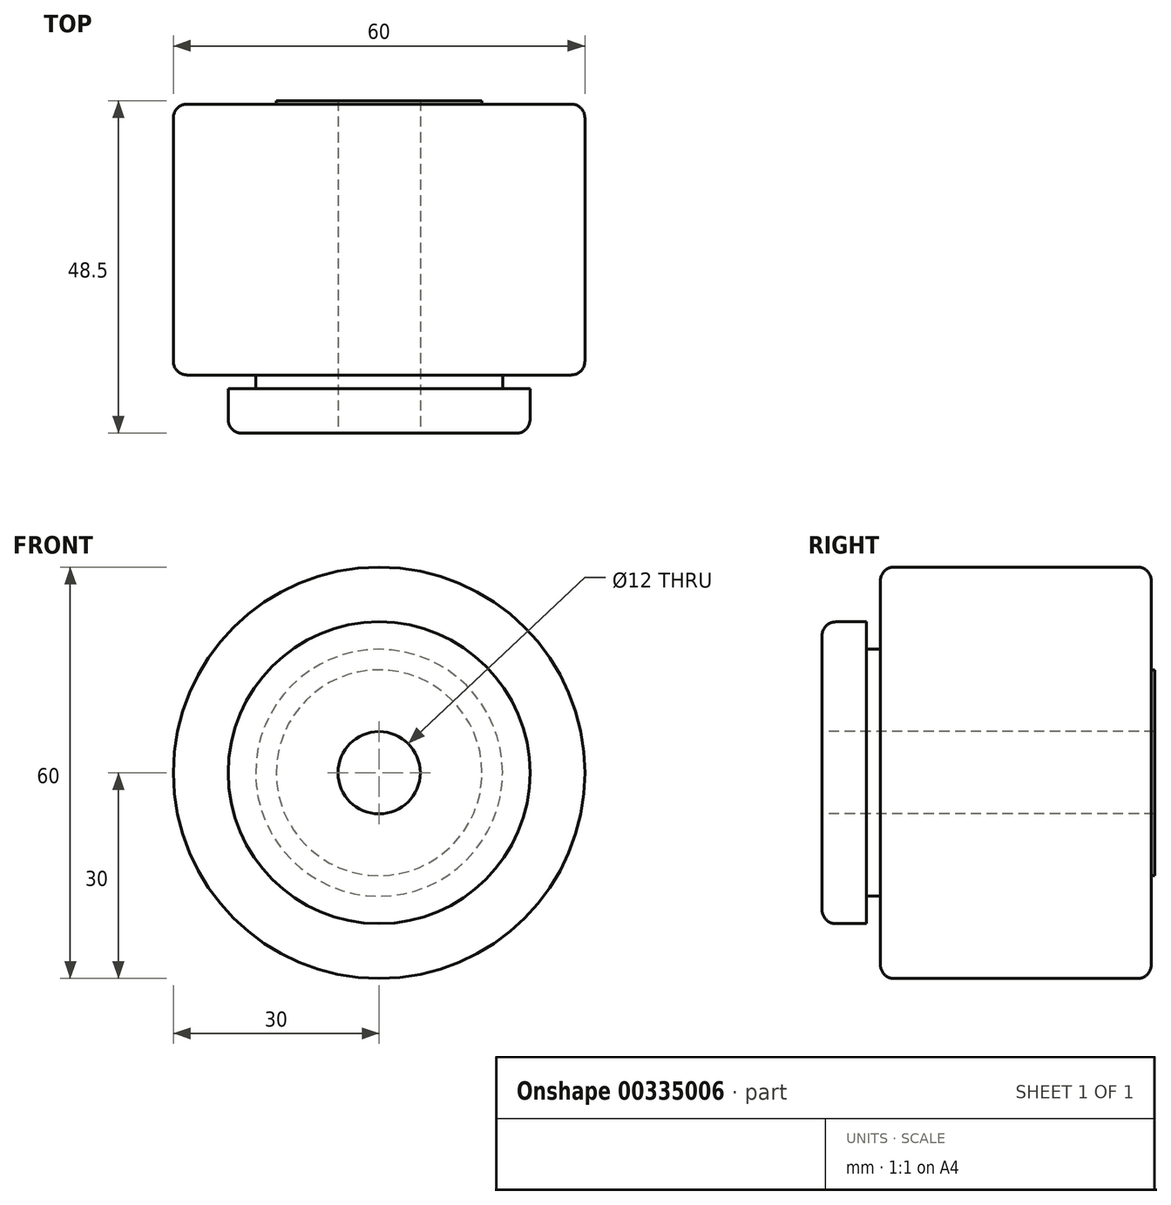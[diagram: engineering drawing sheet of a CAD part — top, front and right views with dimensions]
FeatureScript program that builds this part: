
annotation { "Feature Type Name" : "Feature", "Feature Type Description" : "" }
export const myFeature = defineFeature(function(context is Context, id is Id, definition is map)
    precondition{}
    {
        {
            var Q0;
            Q0=qCreatedBy(makeId("Right.planeOp"),FACE);
            var sketch = newSketch(context, id + "F0", { "sketchPlane" : qUnion([Q0])});
            skLineSegment(sketch, "E0", {"start": v(0, 6) * mm, "end": v(48.5, 6) * mm});
            skLineSegment(sketch, "E1", {"start": v(48.5, 6) * mm, "end": v(48.5, 15) * mm});
            skLineSegment(sketch, "E2", {"start": v(48.5, 15) * mm, "end": v(48, 15) * mm});
            skLineSegment(sketch, "E3", {"start": v(48, 15) * mm, "end": v(48, 30) * mm});
            skLineSegment(sketch, "E4", {"start": v(48, 30) * mm, "end": v(8.5, 30) * mm});
            skLineSegment(sketch, "E5", {"start": v(8.5, 30) * mm, "end": v(8.5, 18) * mm});
            skLineSegment(sketch, "E6", {"start": v(8.5, 18) * mm, "end": v(6.5, 18) * mm});
            skLineSegment(sketch, "E7", {"start": v(6.5, 22) * mm, "end": v(6.5, 18) * mm});
            skLineSegment(sketch, "E8", {"start": v(6.5, 22) * mm, "end": v(0, 22) * mm});
            skLineSegment(sketch, "E9", {"start": v(0, 22) * mm, "end": v(0, 6) * mm});
            skLineSegment(sketch, "E10", {"start": v(-0.36, 0) * mm, "end": v(40, 0) * mm});
            skSolve(sketch);
        }
        {
            var Q0;
            Q0=makeQuery(id+"F0.imprint","IMPRINT",FACE,{"disambiguationData":[TD([[makeQuery(id+"F0.imprint","IMPRINT",EDGE,{"derivedFrom":sQuery(id+"F0.wireOp",EDGE,"E0")}),1.0]])]});
            var Q1;
            Q1=sQuery(id+"F0.wireOp",EDGE,"E10");
            revolve(context, id + "F1", {"entities" : qUnion([Q0]), "axis" : qUnion([Q1]), "revolveType" : RevolveType.FULL});
        }
        {
            var Q0;
            Q0=makeQuery(id+"F1.opRevolve","SWEPT_EDGE",EDGE,{"disambiguationData":[OSD([sQuery(id+"F0.wireOp",EDGE,"E8"),sQuery(id+"F0.wireOp",EDGE,"E9")])]});
            var Q1;
            Q1=makeQuery(id+"F1.opRevolve","SWEPT_EDGE",EDGE,{"disambiguationData":[OSD([sQuery(id+"F0.wireOp",EDGE,"E4"),sQuery(id+"F0.wireOp",EDGE,"E5")])]});
            var Q2;
            Q2=makeQuery(id+"F1.opRevolve","SWEPT_EDGE",EDGE,{"disambiguationData":[OSD([sQuery(id+"F0.wireOp",EDGE,"E3"),sQuery(id+"F0.wireOp",EDGE,"E4")])]});
            fillet(context, id + "F2", {"entities" : qUnion([Q0, Q1, Q2]), "radius" : 2 * mm, "tangentPropagation" : true, "allowEdgeOverflow" : false});
        }
    });
